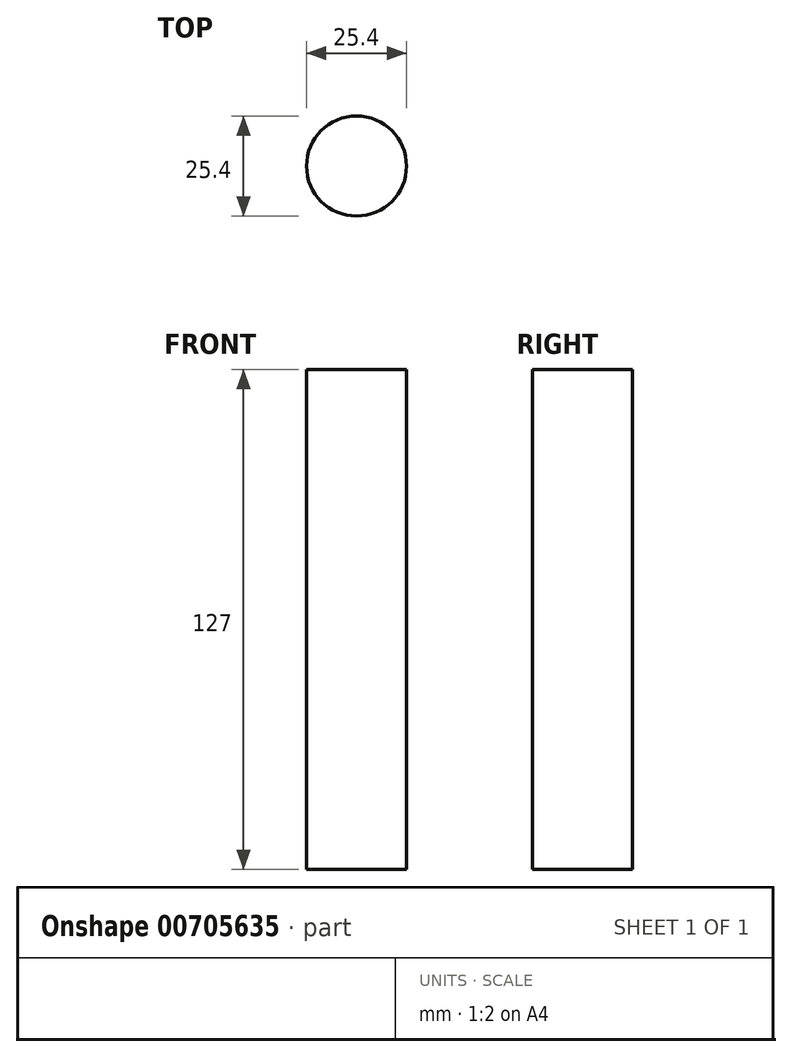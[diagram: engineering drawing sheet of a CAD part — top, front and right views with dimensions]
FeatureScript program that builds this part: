
annotation { "Feature Type Name" : "Feature", "Feature Type Description" : "" }
export const myFeature = defineFeature(function(context is Context, id is Id, definition is map)
    precondition{}
    {
        {
            var Q0;
            Q0=qCreatedBy(makeId("Top.planeOp"),FACE);
            var sketch = newSketch(context, id + "F0", { "sketchPlane" : qUnion([Q0])});
            skCircle(sketch, "E0", {"center": v(0, 0) * mm, "radius": 12.7 * mm});
            skSolve(sketch);
        }
        {
            var Q0;
            Q0 = qSketchRegion(id + "F0", true);
            extrude(context, id + "F1", {"entities" : qUnion([Q0]), "depth" : 127 * mm, "offsetDistance" : 25.4 * mm});
        }
    });
